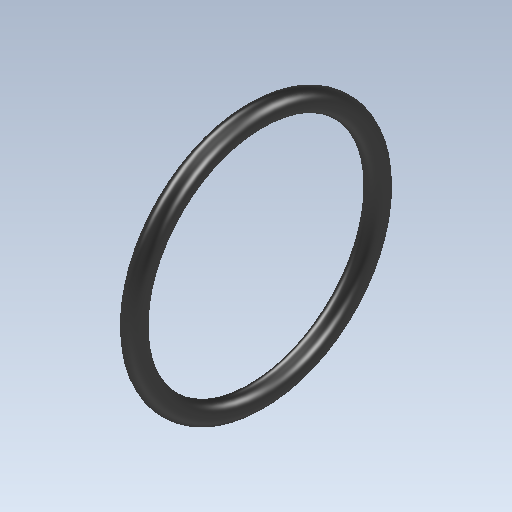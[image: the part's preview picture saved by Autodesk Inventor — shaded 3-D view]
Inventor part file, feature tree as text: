
AUTODESK INVENTOR PART (.ipt)
format: ipt  version: 2021 (Build 250183000, 183)  size: 136,704 bytes
history: native  units: mm
features: revolve x1, sketch x1
ambient origin geometry x8: Origin, YZ Plane, XZ Plane, XY Plane, X Axis, Y Axis, Z Axis, Center Point
bodies: Solid1 (feature_tree)
feature tree (2):
  revolve  "Revolution1"  [1 undecoded]
  sketch  "Sketch1"  dims[d0=24.0mm d1=2.0mm d2=90.0deg]
note: 1 required parameter value undecoded (feature->parameter linkage not recoverable at this tier; creation-order binding heuristic only, values carry confidence <= 0.55)
